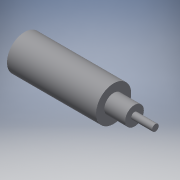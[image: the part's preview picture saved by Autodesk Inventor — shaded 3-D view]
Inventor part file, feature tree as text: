
AUTODESK INVENTOR PART (.ipt)
format: ipt  version: 2016 (Build 200138000, 138)  size: 103,424 bytes
history: native  units: in
note: dims shown in document units (in); Inventor stores cm internally (conversion verified against a paired STEP export)
features: extrude x3, sketch x3
ambient origin geometry x8: Origin, YZ Plane, XZ Plane, XY Plane, X Axis, Y Axis, Z Axis, Center Point
bodies: Solid1 (feature_tree)
feature tree (6):
  extrude  "Extrusion1"  Depth=0.3189in TaperAngle=0.0deg
  extrude  "Extrusion2"  Depth=0.0748in TaperAngle=0.0deg
  extrude  "Extrusion3"  Depth=0.0748in TaperAngle=0.0deg
  sketch  "Sketch1"  dims[d0=0.126in d1=0.3189in d2=0.0in]
  sketch  "Sketch2"  dims[d3=0.0669in d4=0.0748in d5=0.0in]
  sketch  "Sketch3"  dims[d6=0.0236in d7=0.0748in d8=0.0in]
